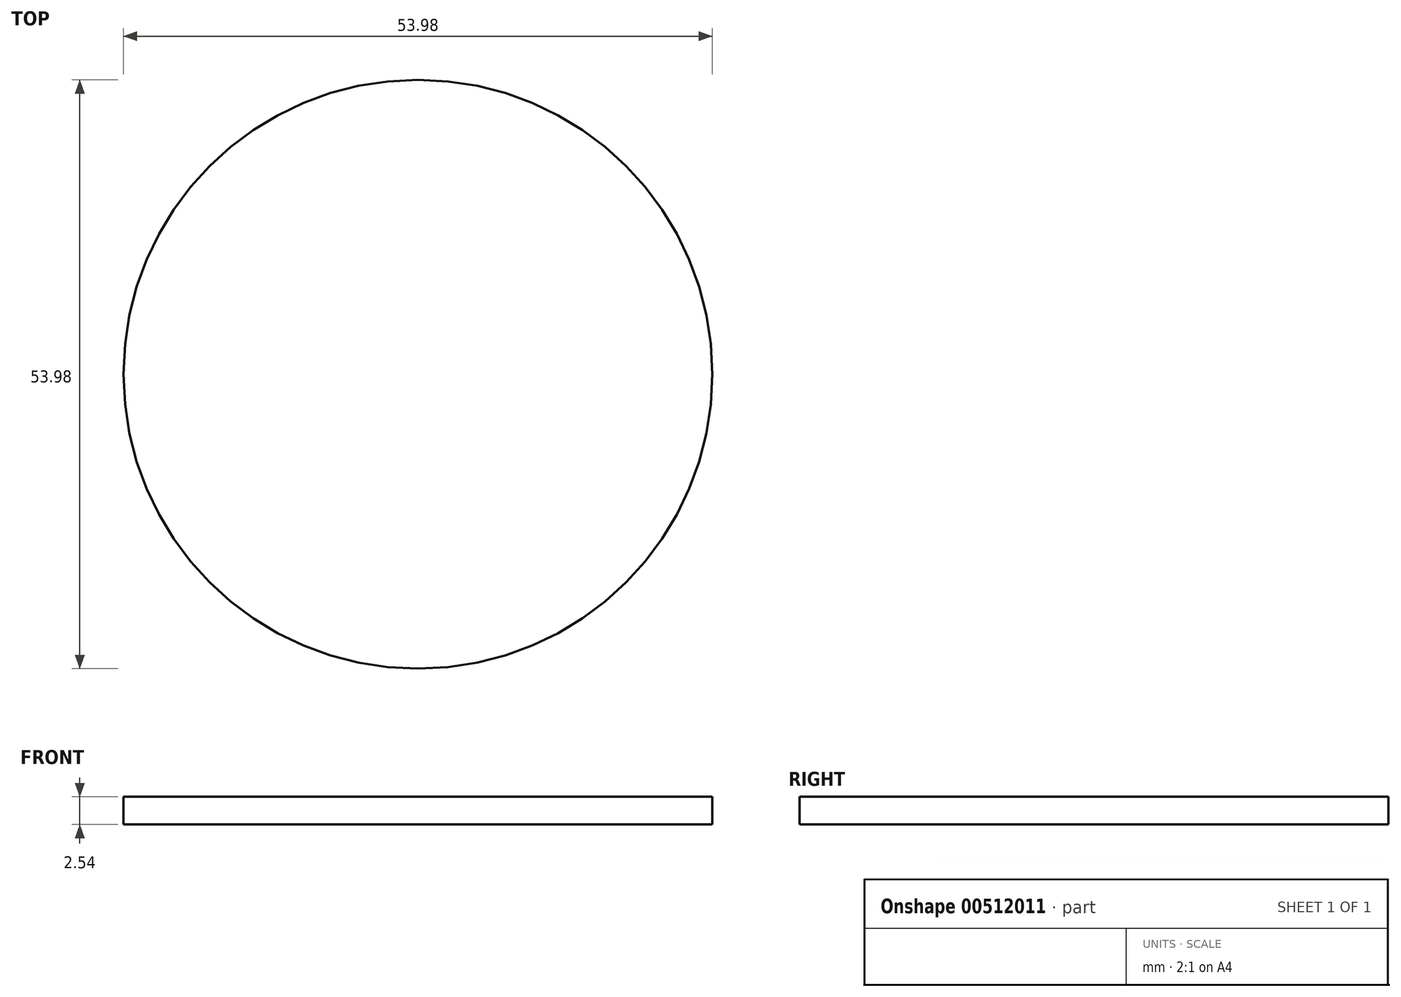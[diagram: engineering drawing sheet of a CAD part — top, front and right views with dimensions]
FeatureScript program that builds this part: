
annotation { "Feature Type Name" : "Feature", "Feature Type Description" : "" }
export const myFeature = defineFeature(function(context is Context, id is Id, definition is map)
    precondition{}
    {
        {
            var Q0;
            Q0=qCreatedBy(makeId("Top.planeOp"),FACE);
            var sketch = newSketch(context, id + "F0", { "sketchPlane" : qUnion([Q0])});
            skCircle(sketch, "E0", {"center": v(0, 0) * mm, "radius": 26.99 * mm});
            skSolve(sketch);
        }
        {
            var Q0;
            Q0=makeQuery(id+"F0.imprint","IMPRINT",FACE,{"disambiguationData":[TD([[makeQuery(id+"F0.imprint","IMPRINT",EDGE,{"derivedFrom":sQuery(id+"F0.wireOp",EDGE,"E0")}),1.0]])]});
            extrude(context, id + "F1", {"entities" : qUnion([Q0]), "depth" : 2.54 * mm});
        }
    });
